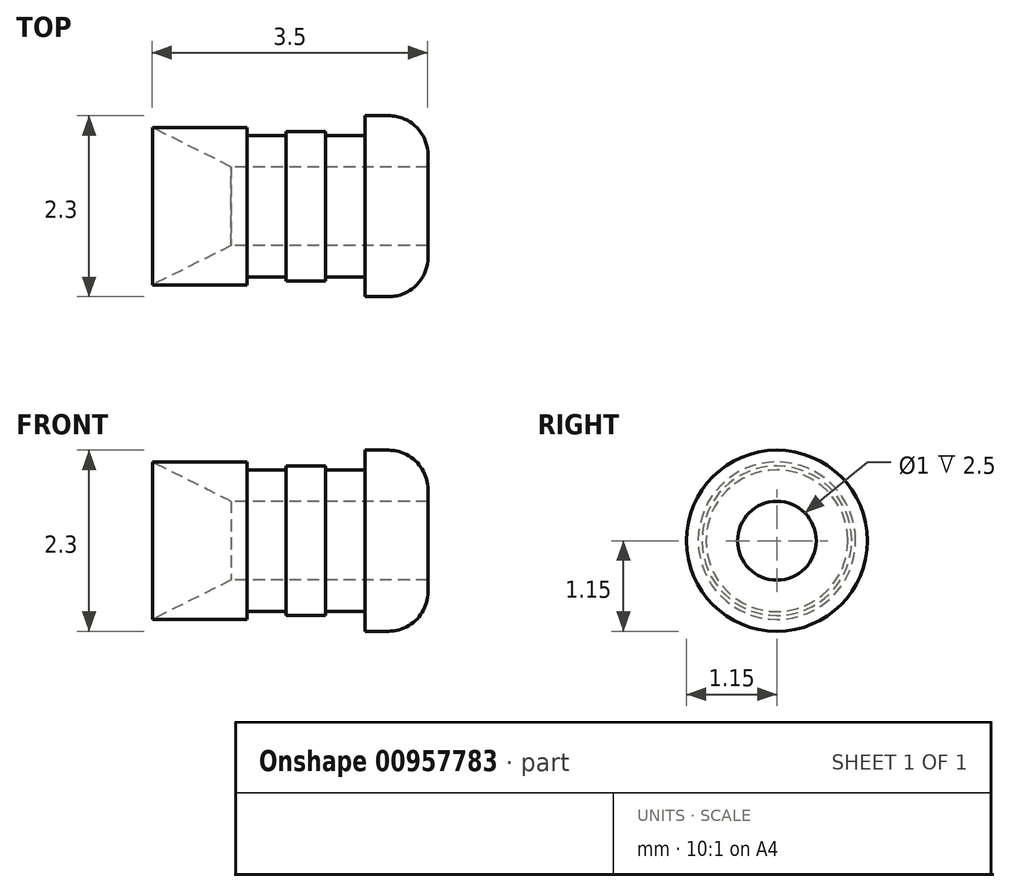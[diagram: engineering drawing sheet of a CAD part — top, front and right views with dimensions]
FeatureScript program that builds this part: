
annotation { "Feature Type Name" : "Feature", "Feature Type Description" : "" }
export const myFeature = defineFeature(function(context is Context, id is Id, definition is map)
    precondition{}
    {
        {
            var Q0;
            Q0=qCreatedBy(makeId("Top.planeOp"),FACE);
            var sketch = newSketch(context, id + "F0", { "sketchPlane" : qUnion([Q0])});
            skLineSegment(sketch, "E0", {"start": v(-3.87, 0) * mm, "end": v(4.1, 0) * mm, "construction": true});
            skLineSegment(sketch, "E1", {"start": v(-1.34, 1) * mm, "end": v(-0.34, 0.5) * mm});
            skLineSegment(sketch, "E2", {"start": v(-0.34, 0.5) * mm, "end": v(2.16, 0.5) * mm});
            skLineSegment(sketch, "E3", {"start": v(2.16, 0.5) * mm, "end": v(2.16, 0.65) * mm});
            skLineSegment(sketch, "E4", {"start": v(1.66, 1.15) * mm, "end": v(1.36, 1.15) * mm});
            skLineSegment(sketch, "E5", {"start": v(1.36, 1.15) * mm, "end": v(1.36, 0.9) * mm});
            skLineSegment(sketch, "E6", {"start": v(1.36, 0.9) * mm, "end": v(0.86, 0.9) * mm});
            skLineSegment(sketch, "E7", {"start": v(0.86, 0.9) * mm, "end": v(0.86, 0.95) * mm});
            skLineSegment(sketch, "E8", {"start": v(0.86, 0.95) * mm, "end": v(0.36, 0.95) * mm});
            skLineSegment(sketch, "E9", {"start": v(0.36, 0.95) * mm, "end": v(0.36, 0.9) * mm});
            skLineSegment(sketch, "E10", {"start": v(0.36, 0.9) * mm, "end": v(-0.14, 0.9) * mm});
            skLineSegment(sketch, "E11", {"start": v(-0.14, 0.9) * mm, "end": v(-0.14, 1) * mm});
            skLineSegment(sketch, "E12", {"start": v(-0.14, 1) * mm, "end": v(-1.34, 1) * mm});
            skPoint(sketch, "E13.visualSharp", {"position": v(2.16, 1.15) * mm});
            skArc(sketch, "E13.filletArc", {"start": v(2.16, 0.65) * mm, "mid": v(2.02, 1) * mm, "end": v(1.66, 1.15) * mm});
            skSolve(sketch);
        }
        {
            var Q0;
            Q0 = qSketchRegion(id + "F0", true);
            var Q1;
            Q1=sQuery(id+"F0.wireOp",EDGE,"E0");
            revolve(context, id + "F1", {"surfaceOperationType" : NewSurfaceOperationType.NEW, "entities" : qUnion([Q0]), "axis" : qUnion([Q1]), "revolveType" : RevolveType.FULL});
        }
    });
